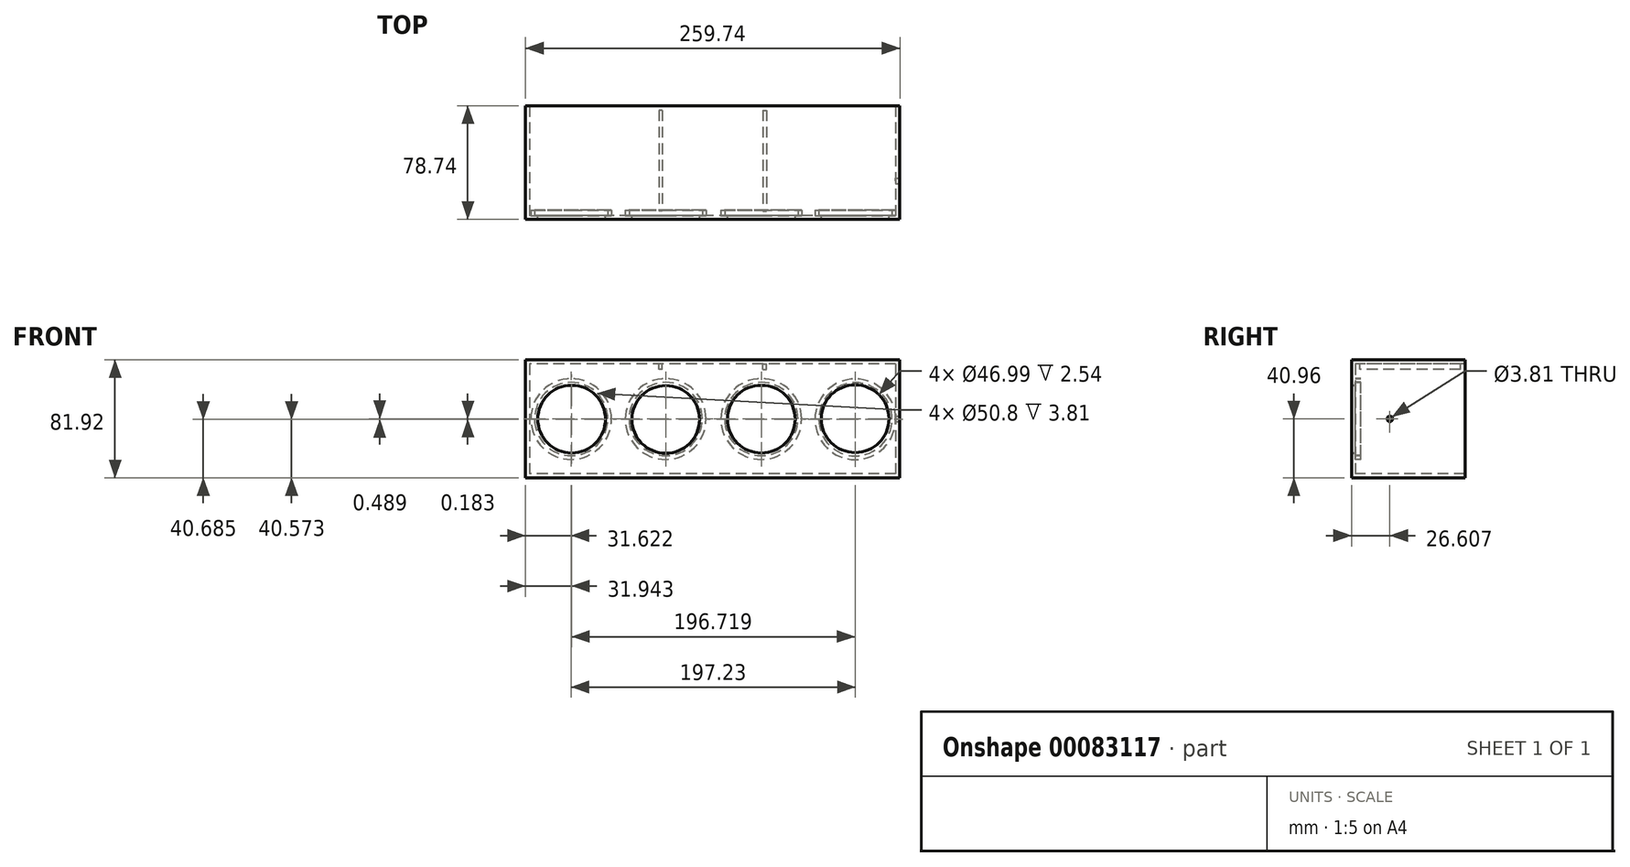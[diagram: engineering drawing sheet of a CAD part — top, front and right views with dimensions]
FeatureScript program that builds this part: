
annotation { "Feature Type Name" : "Feature", "Feature Type Description" : "" }
export const myFeature = defineFeature(function(context is Context, id is Id, definition is map)
    precondition{}
    {
        {
            var Q0;
            Q0=qCreatedBy(makeId("Front.planeOp"),FACE);
            var sketch = newSketch(context, id + "F0", { "sketchPlane" : qUnion([Q0])});
            skLineSegment(sketch, "E0.bottom", {"start": v(127, 38.1) * mm, "end": v(-127, 38.1) * mm});
            skLineSegment(sketch, "E0.top", {"start": v(127, -38.1) * mm, "end": v(-127, -38.1) * mm});
            skLineSegment(sketch, "E0.left", {"start": v(127, 38.1) * mm, "end": v(127, -38.1) * mm});
            skLineSegment(sketch, "E0.right", {"start": v(-127, 38.1) * mm, "end": v(-127, -38.1) * mm});
            skPoint(sketch, "E0.middle", {"position": v(0, 0) * mm});
            skLineSegment(sketch, "E1", {"start": v(-127, 0) * mm, "end": v(0, 0) * mm});
            skLineSegment(sketch, "E2", {"start": v(0, 0) * mm, "end": v(127, 0) * mm});
            skLineSegment(sketch, "E3.bottom", {"start": v(129.87, 40.96) * mm, "end": v(-129.87, 40.96) * mm});
            skLineSegment(sketch, "E3.top", {"start": v(129.87, -40.96) * mm, "end": v(-129.87, -40.96) * mm});
            skLineSegment(sketch, "E3.left", {"start": v(129.87, 40.96) * mm, "end": v(129.87, -40.96) * mm});
            skLineSegment(sketch, "E3.right", {"start": v(-129.87, 40.96) * mm, "end": v(-129.87, -40.96) * mm});
            skLineSegment(sketch, "E4", {"start": v(127, 0) * mm, "end": v(63.5, 0) * mm});
            skLineSegment(sketch, "E5", {"start": v(63.5, 0) * mm, "end": v(0, 0) * mm});
            skLineSegment(sketch, "E6", {"start": v(0, 0) * mm, "end": v(-63.5, 0) * mm});
            skLineSegment(sketch, "E7", {"start": v(-63.5, 0) * mm, "end": v(-127, 0) * mm});
            skCircle(sketch, "E8", {"center": v(33.7, -0.14) * mm, "radius": 23.5 * mm});
            skCircle(sketch, "E9", {"center": v(-32.6, -0.39) * mm, "radius": 23.5 * mm});
            skCircle(sketch, "E10", {"center": v(-97.93, -0.14) * mm, "radius": 23.5 * mm});
            skCircle(sketch, "E11", {"center": v(98.8, 0.1) * mm, "radius": 23.5 * mm});
            skSolve(sketch);
        }
        {
            var Q0;
            {var subQ3=sQuery(id+"F0.wireOp",EDGE,"E0.bottom");Q0=makeQuery(id+"F0.imprint","IMPRINT",FACE,{"disambiguationData":[TD([[makeQuery(id+"F0.imprint","IMPRINT",EDGE,{"derivedFrom":subQ3}),-1.0]])]});}
            var Q1;
            {var subQ5=sQuery(id+"F0.wireOp",EDGE,"E0.bottom");Q1=makeQuery(id+"F0.imprint","IMPRINT",FACE,{"disambiguationData":[TD([[makeQuery(id+"F0.imprint","IMPRINT",EDGE,{"derivedFrom":subQ5}),1.0]])]});}
            var Q2;
            {var subQ6=sQuery(id+"F0.wireOp",EDGE,"E0.top");Q2=makeQuery(id+"F0.imprint","IMPRINT",FACE,{"disambiguationData":[TD([[makeQuery(id+"F0.imprint","IMPRINT",EDGE,{"derivedFrom":subQ6}),-1.0]])]});}
            extrude(context, id + "F1", {"entities" : qUnion([Q0, Q1, Q2]), "depth" : 2.54 * mm});
        }
        {
            var Q0;
            {var subQ3=sQuery(id+"F0.wireOp",EDGE,"E0.bottom");Q0=makeQuery(id+"F0.imprint","IMPRINT",FACE,{"disambiguationData":[TD([[makeQuery(id+"F0.imprint","IMPRINT",EDGE,{"derivedFrom":subQ3}),-1.0]])]});}
            extrude(context, id + "F2", {"entities" : qUnion([Q0]), "operationType" : NewBodyOperationType.ADD, "oppositeDirection" : true, "depth" : 76.2 * mm});
        }
        {
            var Q0;
            {var subQ5=sQuery(id+"F0.wireOp",EDGE,"E0.bottom");Q0=makeQuery(id+"F0.imprint","IMPRINT",FACE,{"disambiguationData":[TD([[makeQuery(id+"F0.imprint","IMPRINT",EDGE,{"derivedFrom":subQ5}),1.0]])]});}
            var sketch = newSketch(context, id + "F3", { "sketchPlane" : qUnion([Q0])});
            skCircle(sketch, "E12", {"center": v(-32.63, -0.1) * mm, "radius": 25.4 * mm});
            skCircle(sketch, "E13", {"center": v(-32.63, -0.1) * mm, "radius": 28 * mm});
            skCircle(sketch, "E14", {"center": v(-98.25, -0.1) * mm, "radius": 25.4 * mm});
            skCircle(sketch, "E15", {"center": v(-98.25, -0.1) * mm, "radius": 28 * mm});
            skCircle(sketch, "E16", {"center": v(33.73, -0.1) * mm, "radius": 25.4 * mm});
            skCircle(sketch, "E17", {"center": v(33.73, -0.1) * mm, "radius": 28 * mm});
            skCircle(sketch, "E18", {"center": v(98.98, -0.27) * mm, "radius": 25.4 * mm});
            skCircle(sketch, "E19", {"center": v(98.98, -0.27) * mm, "radius": 28 * mm});
            skSolve(sketch);
        }
        {
            var Q0;
            {var subQ0=sQuery(id+"F3.wireOp",EDGE,"E18");var subQ1=sQuery(id+"F0.wireOp",EDGE,"E4");var subQ3=makeQuery(id+"F0.imprint","IMPRINT",EDGE,{"disambiguationData":[TD([[makeQuery(id+"F0.imprint","INTERSECT",VERTEX,{"derivedFrom":[sQuery(id+"F0.wireOp",EDGE,"E0.left"),subQ1]}),-1.0]])],"derivedFrom":subQ1});var subQ4=makeQuery(id+"F3.imprint","INTERSECT",VERTEX,{"derivedFrom":[subQ3,subQ0]});Q0=makeQuery(id+"F3.imprint","IMPRINT",FACE,{"disambiguationData":[TD([[makeQuery(id+"F3.imprint","IMPRINT",EDGE,{"disambiguationData":[TD([[subQ4,-1.0]])],"derivedFrom":subQ0}),-1.0]])]});}
            var Q1;
            {var subQ0=sQuery(id+"F3.wireOp",EDGE,"E18");var subQ1=sQuery(id+"F0.wireOp",EDGE,"E4");var subQ3=makeQuery(id+"F0.imprint","IMPRINT",EDGE,{"disambiguationData":[TD([[makeQuery(id+"F0.imprint","INTERSECT",VERTEX,{"derivedFrom":[sQuery(id+"F0.wireOp",EDGE,"E0.left"),subQ1]}),-1.0]])],"derivedFrom":subQ1});var subQ4=makeQuery(id+"F3.imprint","INTERSECT",VERTEX,{"derivedFrom":[subQ3,subQ0]});Q1=makeQuery(id+"F3.imprint","IMPRINT",FACE,{"disambiguationData":[TD([[makeQuery(id+"F3.imprint","IMPRINT",EDGE,{"disambiguationData":[TD([[subQ4,1.0]])],"derivedFrom":subQ0}),-1.0]])]});}
            var Q2;
            {var subQ0=sQuery(id+"F3.wireOp",EDGE,"E16");var subQ1=sQuery(id+"F0.wireOp",EDGE,"E5");var subQ3=makeQuery(id+"F0.imprint","IMPRINT",EDGE,{"disambiguationData":[TD([[makeQuery(id+"F0.imprint","INTERSECT",VERTEX,{"derivedFrom":[sQuery(id+"F0.wireOp",EDGE,"E4"),subQ1]}),-1.0]])],"derivedFrom":subQ1});var subQ4=makeQuery(id+"F3.imprint","INTERSECT",VERTEX,{"derivedFrom":[subQ3,subQ0]});Q2=makeQuery(id+"F3.imprint","IMPRINT",FACE,{"disambiguationData":[TD([[makeQuery(id+"F3.imprint","IMPRINT",EDGE,{"disambiguationData":[TD([[subQ4,1.0]])],"derivedFrom":subQ0}),-1.0]])]});}
            var Q3;
            {var subQ0=sQuery(id+"F3.wireOp",EDGE,"E16");var subQ1=sQuery(id+"F0.wireOp",EDGE,"E5");var subQ3=makeQuery(id+"F0.imprint","IMPRINT",EDGE,{"disambiguationData":[TD([[makeQuery(id+"F0.imprint","INTERSECT",VERTEX,{"derivedFrom":[sQuery(id+"F0.wireOp",EDGE,"E4"),subQ1]}),-1.0]])],"derivedFrom":subQ1});var subQ4=makeQuery(id+"F3.imprint","INTERSECT",VERTEX,{"derivedFrom":[subQ3,subQ0]});Q3=makeQuery(id+"F3.imprint","IMPRINT",FACE,{"disambiguationData":[TD([[makeQuery(id+"F3.imprint","IMPRINT",EDGE,{"disambiguationData":[TD([[subQ4,-1.0]])],"derivedFrom":subQ0}),-1.0]])]});}
            var Q4;
            {var subQ0=sQuery(id+"F3.wireOp",EDGE,"E12");var subQ1=sQuery(id+"F0.wireOp",EDGE,"E6");var subQ3=makeQuery(id+"F0.imprint","IMPRINT",EDGE,{"disambiguationData":[TD([[makeQuery(id+"F0.imprint","INTERSECT",VERTEX,{"derivedFrom":[sQuery(id+"F0.wireOp",EDGE,"E5"),subQ1]}),-1.0]])],"derivedFrom":subQ1});var subQ4=makeQuery(id+"F3.imprint","INTERSECT",VERTEX,{"derivedFrom":[subQ3,subQ0]});Q4=makeQuery(id+"F3.imprint","IMPRINT",FACE,{"disambiguationData":[TD([[makeQuery(id+"F3.imprint","IMPRINT",EDGE,{"disambiguationData":[TD([[subQ4,1.0]])],"derivedFrom":subQ0}),-1.0]])]});}
            var Q5;
            {var subQ0=sQuery(id+"F3.wireOp",EDGE,"E12");var subQ1=sQuery(id+"F0.wireOp",EDGE,"E6");var subQ3=makeQuery(id+"F0.imprint","IMPRINT",EDGE,{"disambiguationData":[TD([[makeQuery(id+"F0.imprint","INTERSECT",VERTEX,{"derivedFrom":[sQuery(id+"F0.wireOp",EDGE,"E5"),subQ1]}),-1.0]])],"derivedFrom":subQ1});var subQ4=makeQuery(id+"F3.imprint","INTERSECT",VERTEX,{"derivedFrom":[subQ3,subQ0]});Q5=makeQuery(id+"F3.imprint","IMPRINT",FACE,{"disambiguationData":[TD([[makeQuery(id+"F3.imprint","IMPRINT",EDGE,{"disambiguationData":[TD([[subQ4,-1.0]])],"derivedFrom":subQ0}),-1.0]])]});}
            var Q6;
            {var subQ0=sQuery(id+"F3.wireOp",EDGE,"E14");var subQ1=sQuery(id+"F0.wireOp",EDGE,"E7");var subQ3=makeQuery(id+"F0.imprint","IMPRINT",EDGE,{"disambiguationData":[TD([[makeQuery(id+"F0.imprint","INTERSECT",VERTEX,{"derivedFrom":[sQuery(id+"F0.wireOp",EDGE,"E6"),subQ1]}),-1.0]])],"derivedFrom":subQ1});var subQ4=makeQuery(id+"F3.imprint","INTERSECT",VERTEX,{"derivedFrom":[subQ3,subQ0]});Q6=makeQuery(id+"F3.imprint","IMPRINT",FACE,{"disambiguationData":[TD([[makeQuery(id+"F3.imprint","IMPRINT",EDGE,{"disambiguationData":[TD([[subQ4,-1.0]])],"derivedFrom":subQ0}),-1.0]])]});}
            var Q7;
            {var subQ0=sQuery(id+"F3.wireOp",EDGE,"E14");var subQ1=sQuery(id+"F0.wireOp",EDGE,"E7");var subQ3=makeQuery(id+"F0.imprint","IMPRINT",EDGE,{"disambiguationData":[TD([[makeQuery(id+"F0.imprint","INTERSECT",VERTEX,{"derivedFrom":[sQuery(id+"F0.wireOp",EDGE,"E6"),subQ1]}),-1.0]])],"derivedFrom":subQ1});var subQ4=makeQuery(id+"F3.imprint","INTERSECT",VERTEX,{"derivedFrom":[subQ3,subQ0]});Q7=makeQuery(id+"F3.imprint","IMPRINT",FACE,{"disambiguationData":[TD([[makeQuery(id+"F3.imprint","IMPRINT",EDGE,{"disambiguationData":[TD([[subQ4,1.0]])],"derivedFrom":subQ0}),-1.0]])]});}
            extrude(context, id + "F4", {"entities" : qUnion([Q0, Q1, Q2, Q3, Q4, Q5, Q6, Q7]), "operationType" : NewBodyOperationType.ADD, "oppositeDirection" : true, "depth" : 3.8 * mm});
        }
        {
            var Q0;
            {var subQ0=sQuery(id+"F0.wireOp",EDGE,"E3.left");Q0=makeQuery(id+"F2.boolean.opBoolean","MERGE",FACE,{"derivedFrom":[makeQuery(id+"F1.opExtrude","SWEPT_FACE",FACE,{"disambiguationData":[OSD([subQ0])]}),makeQuery(id+"F2.opExtrude","SWEPT_FACE",FACE,{"disambiguationData":[OSD([subQ0])]})]});}
            var sketch = newSketch(context, id + "F5", { "sketchPlane" : qUnion([Q0])});
            skCircle(sketch, "E20", {"center": v(24.07, 0) * mm, "radius": 1.9 * mm});
            skSolve(sketch);
        }
        {
            var Q0;
            Q0=makeQuery(id+"F5.imprint","IMPRINT",FACE,{"disambiguationData":[TD([[makeQuery(id+"F5.imprint","IMPRINT",EDGE,{"derivedFrom":sQuery(id+"F5.wireOp",EDGE,"E20")}),1.0]])]});
            extrude(context, id + "F6", {"entities" : qUnion([Q0]), "operationType" : NewBodyOperationType.REMOVE, "oppositeDirection" : true, "depth" : 25.4 * mm});
        }
        {
            var Q0;
            Q0=makeQuery(id+"F2.opExtrude","SWEPT_FACE",FACE,{"disambiguationData":[OSD([sQuery(id+"F0.wireOp",EDGE,"E0.bottom")])]});
            var sketch = newSketch(context, id + "F7", { "sketchPlane" : qUnion([Q0])});
            skLineSegment(sketch, "E21.left", {"start": v(34.93, -73.14) * mm, "end": v(34.92, -3.3) * mm});
            skLineSegment(sketch, "E21.right", {"start": v(-34.93, -73.14) * mm, "end": v(-34.93, -3.3) * mm});
            skPoint(sketch, "E21.middle", {"position": v(0, -38.22) * mm});
            skLineSegment(sketch, "E22.bottom", {"start": v(-34.93, -73.14) * mm, "end": v(-37.2, -73.14) * mm});
            skLineSegment(sketch, "E22.top", {"start": v(-34.93, -3.2) * mm, "end": v(-37.2, -3.2) * mm});
            skLineSegment(sketch, "E22.left", {"start": v(-34.93, -73.14) * mm, "end": v(-34.93, -3.2) * mm});
            skLineSegment(sketch, "E22.right", {"start": v(-37.2, -73.14) * mm, "end": v(-37.2, -3.2) * mm});
            skLineSegment(sketch, "E23.bottom", {"start": v(34.93, -73.14) * mm, "end": v(37.4, -73.14) * mm});
            skLineSegment(sketch, "E23.top", {"start": v(34.93, -3.3) * mm, "end": v(37.4, -3.3) * mm});
            skLineSegment(sketch, "E23.left", {"start": v(34.93, -73.14) * mm, "end": v(34.93, -3.3) * mm});
            skLineSegment(sketch, "E23.right", {"start": v(37.4, -73.14) * mm, "end": v(37.4, -3.3) * mm});
            skSolve(sketch);
        }
        {
            var Q0;
            {var subQ3=sQuery(id+"F7.wireOp",EDGE,"E22.bottom");Q0=makeQuery(id+"F7.imprint","IMPRINT",FACE,{"disambiguationData":[TD([[makeQuery(id+"F7.imprint","IMPRINT",EDGE,{"derivedFrom":subQ3}),-1.0]])]});}
            var Q1;
            Q1=makeQuery(id+"F7.imprint","IMPRINT",FACE,{"disambiguationData":[TD([[makeQuery(id+"F7.imprint","IMPRINT",EDGE,{"derivedFrom":sQuery(id+"F7.wireOp",EDGE,"E23.bottom")}),1.0]])]});
            extrude(context, id + "F8", {"entities" : qUnion([Q0, Q1]), "operationType" : NewBodyOperationType.ADD, "depth" : 3.8 * mm});
        }
    });
